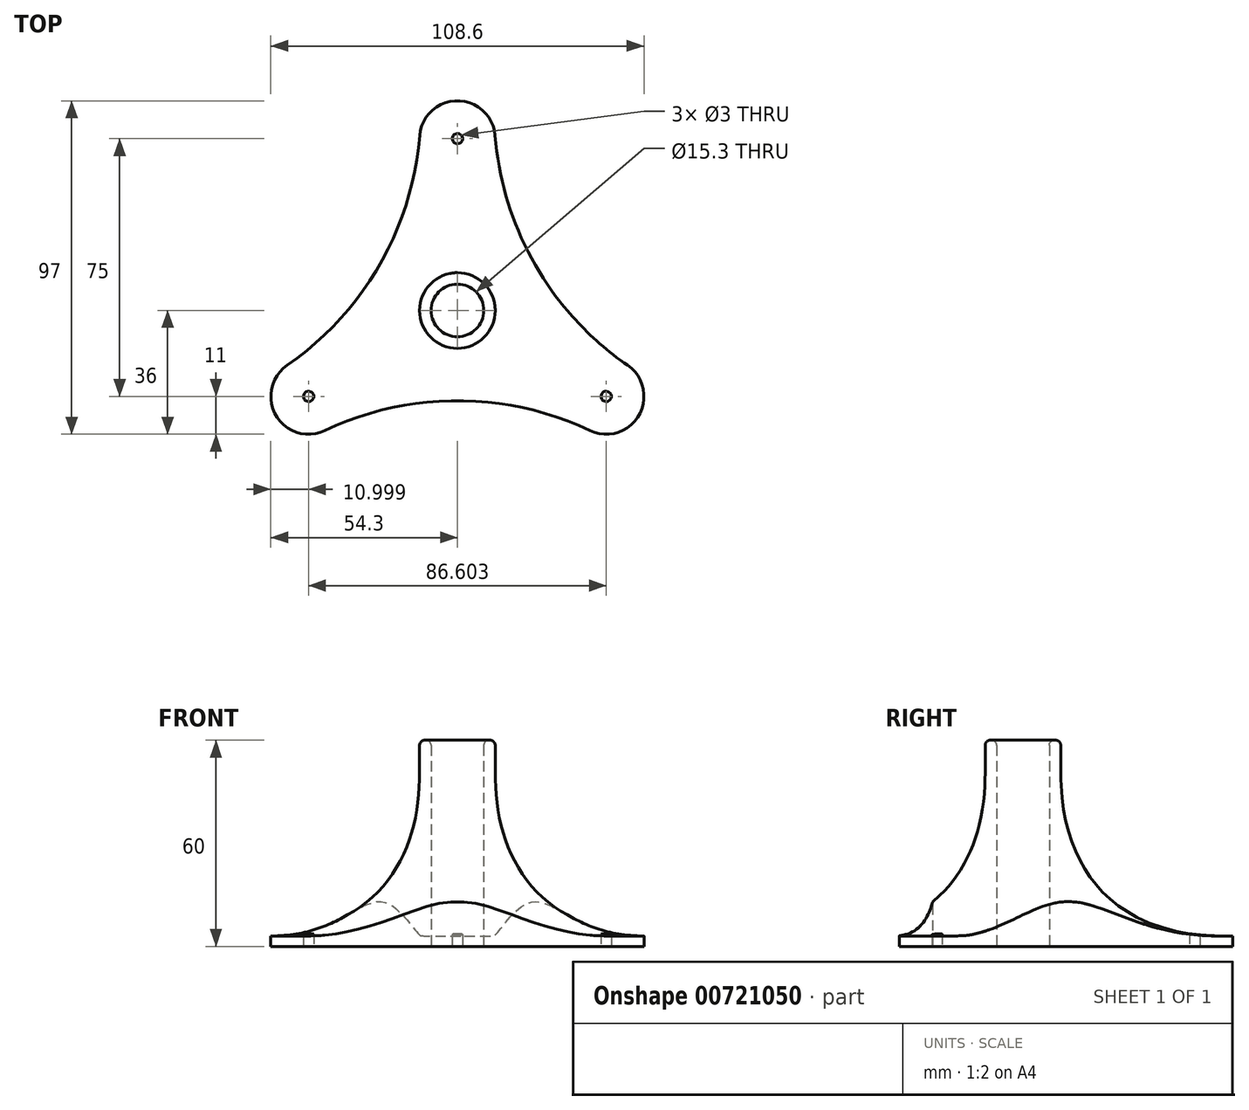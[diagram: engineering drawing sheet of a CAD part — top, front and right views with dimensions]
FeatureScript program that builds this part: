
annotation { "Feature Type Name" : "Feature", "Feature Type Description" : "" }
export const myFeature = defineFeature(function(context is Context, id is Id, definition is map)
    precondition{}
    {
        {
            var Q0;
            Q0=qCreatedBy(makeId("Top.planeOp"),FACE);
            var sketch = newSketch(context, id + "F0", { "sketchPlane" : qUnion([Q0])});
            skLineSegment(sketch, "E0", {"start": v(0, 0) * mm, "end": v(0, 50) * mm, "construction": true});
            skCircle(sketch, "E1", {"center": v(0, 0) * mm, "radius": 7.65 * mm});
            skArc(sketch, "E2.0.startCap", {"start": v(11, 0) * mm, "mid": v(0, -11) * mm, "end": v(-11, 0) * mm});
            skArc(sketch, "E2.0.endCap", {"start": v(-11, 50) * mm, "mid": v(0, 61) * mm, "end": v(11, 50) * mm});
            skLineSegment(sketch, "E2.0.left", {"start": v(-11, 0) * mm, "end": v(-11, 50) * mm});
            skLineSegment(sketch, "E2.0.right", {"start": v(11, 0) * mm, "end": v(11, 50) * mm});
            skArc(sketch, "E3.1.0", {"start": v(-5.5, 9.53) * mm, "mid": v(9.53, 5.5) * mm, "end": v(5.5, -9.53) * mm});
            skLineSegment(sketch, "E3.1.1", {"start": v(-5.5, 9.53) * mm, "end": v(-48.8, -15.47) * mm});
            skLineSegment(sketch, "E3.1.2", {"start": v(5.5, -9.53) * mm, "end": v(-37.8, -34.53) * mm});
            skArc(sketch, "E3.1.3", {"start": v(-37.8, -34.53) * mm, "mid": v(-52.83, -30.5) * mm, "end": v(-48.8, -15.47) * mm});
            skArc(sketch, "E3.2.0", {"start": v(-5.5, -9.53) * mm, "mid": v(-9.53, 5.5) * mm, "end": v(5.5, 9.53) * mm});
            skLineSegment(sketch, "E3.2.1", {"start": v(-5.5, -9.53) * mm, "end": v(37.8, -34.53) * mm});
            skLineSegment(sketch, "E3.2.2", {"start": v(5.5, 9.53) * mm, "end": v(48.8, -15.47) * mm});
            skArc(sketch, "E3.2.3", {"start": v(48.8, -15.47) * mm, "mid": v(52.83, -30.5) * mm, "end": v(37.8, -34.53) * mm});
            skCircle(sketch, "E4", {"center": v(0, 50) * mm, "radius": 1.5 * mm});
            skCircle(sketch, "E5.1.0", {"center": v(-43.3, -25) * mm, "radius": 1.5 * mm});
            skCircle(sketch, "E5.2.0", {"center": v(43.3, -25) * mm, "radius": 1.5 * mm});
            skSolve(sketch);
        }
        {
            var Q0;
            Q0 = qSketchRegion(id + "F0", true);
            var Q1;
            Q1=makeQuery(id+"F0.imprint","IMPRINT",FACE,{"disambiguationData":[TD([[makeQuery(id+"F0.imprint","IMPRINT",EDGE,{"derivedFrom":sQuery(id+"F0.wireOp",EDGE,"E1")}),-1.0]])]});
            extrude(context, id + "F1", {"entities" : qUnion([Q0, Q1]), "depth" : 3 * mm, "offsetDistance" : 25 * mm});
        }
        {
            var Q0;
            Q0=makeQuery(id+"F1.opExtrude","SWEPT_EDGE",EDGE,{"disambiguationData":[OSD([sQuery(id+"F0.wireOp",EDGE,"E2.0.left"),sQuery(id+"F0.wireOp",EDGE,"E3.1.1")])]});
            var Q1;
            Q1=makeQuery(id+"F1.opExtrude","SWEPT_EDGE",EDGE,{"disambiguationData":[OSD([sQuery(id+"F0.wireOp",EDGE,"E2.0.right"),sQuery(id+"F0.wireOp",EDGE,"E3.2.2")])]});
            var Q2;
            Q2=makeQuery(id+"F1.opExtrude","SWEPT_EDGE",EDGE,{"disambiguationData":[OSD([sQuery(id+"F0.wireOp",EDGE,"E3.1.2"),sQuery(id+"F0.wireOp",EDGE,"E3.2.1")])]});
            fillet(context, id + "F2", {"entities" : qUnion([Q0, Q1, Q2]), "tangentPropagation" : true, "radius" : 90 * mm, "defaultsChanged" : true, "vertexSettings" : [], "allowEdgeOverflow" : false});
        }
        {
            var Q0;
            Q0=makeQuery(id+"F0.imprint","IMPRINT",FACE,{"disambiguationData":[TD([[makeQuery(id+"F0.imprint","IMPRINT",EDGE,{"derivedFrom":sQuery(id+"F0.wireOp",EDGE,"E1")}),-1.0]])]});
            extrude(context, id + "F3", {"entities" : qUnion([Q0]), "operationType" : NewBodyOperationType.ADD, "depth" : 60 * mm, "offsetDistance" : 25 * mm});
        }
        {
            var Q0;
            Q0=makeQuery(id+"F3.boolean.opBoolean","INTERSECT",EDGE,{"derivedFrom":[makeQuery(id+"F1.opExtrude","CAP_FACE",FACE,{"disambiguationData":[OSD([sQuery(id+"F0.wireOp",EDGE,"E1"),sQuery(id+"F0.wireOp",EDGE,"E2.0.endCap"),sQuery(id+"F0.wireOp",EDGE,"E2.0.left"),sQuery(id+"F0.wireOp",EDGE,"E2.0.right"),sQuery(id+"F0.wireOp",EDGE,"E3.1.1"),sQuery(id+"F0.wireOp",EDGE,"E3.1.2"),sQuery(id+"F0.wireOp",EDGE,"E3.1.3"),sQuery(id+"F0.wireOp",EDGE,"E3.2.1"),sQuery(id+"F0.wireOp",EDGE,"E3.2.2"),sQuery(id+"F0.wireOp",EDGE,"E3.2.3"),sQuery(id+"F0.wireOp",EDGE,"E4"),sQuery(id+"F0.wireOp",EDGE,"E5.1.0"),sQuery(id+"F0.wireOp",EDGE,"E5.2.0")])],"isStart":false}),makeQuery(id+"F3.opExtrude","SWEPT_FACE",FACE,{"disambiguationData":[OSD([sQuery(id+"F0.wireOp",EDGE,"E2.0.startCap"),sQuery(id+"F0.wireOp",EDGE,"E3.1.0"),sQuery(id+"F0.wireOp",EDGE,"E3.2.0")])]})]});
            fillet(context, id + "F4", {"entities" : qUnion([Q0]), "tangentPropagation" : true, "crossSection" : FilletCrossSection.CURVATURE, "radius" : 50 * mm, "magnitude" : 0.5, "defaultsChanged" : true, "vertexSettings" : []});
        }
        {
            var Q0;
            Q0=makeQuery(id+"F3.opExtrude","CAP_EDGE",EDGE,{"disambiguationData":[OSD([sQuery(id+"F0.wireOp",EDGE,"E2.0.startCap"),sQuery(id+"F0.wireOp",EDGE,"E3.1.0"),sQuery(id+"F0.wireOp",EDGE,"E3.2.0")])],"isStart":false});
            var Q1;
            Q1=makeQuery(id+"F3.opExtrude","CAP_EDGE",EDGE,{"disambiguationData":[OSD([sQuery(id+"F0.wireOp",EDGE,"E1")])],"isStart":false});
            fillet(context, id + "F5", {"entities" : qUnion([Q0, Q1]), "tangentPropagation" : true, "radius" : 1.5 * mm, "defaultsChanged" : true, "vertexSettings" : [], "allowEdgeOverflow" : false});
        }
    });
